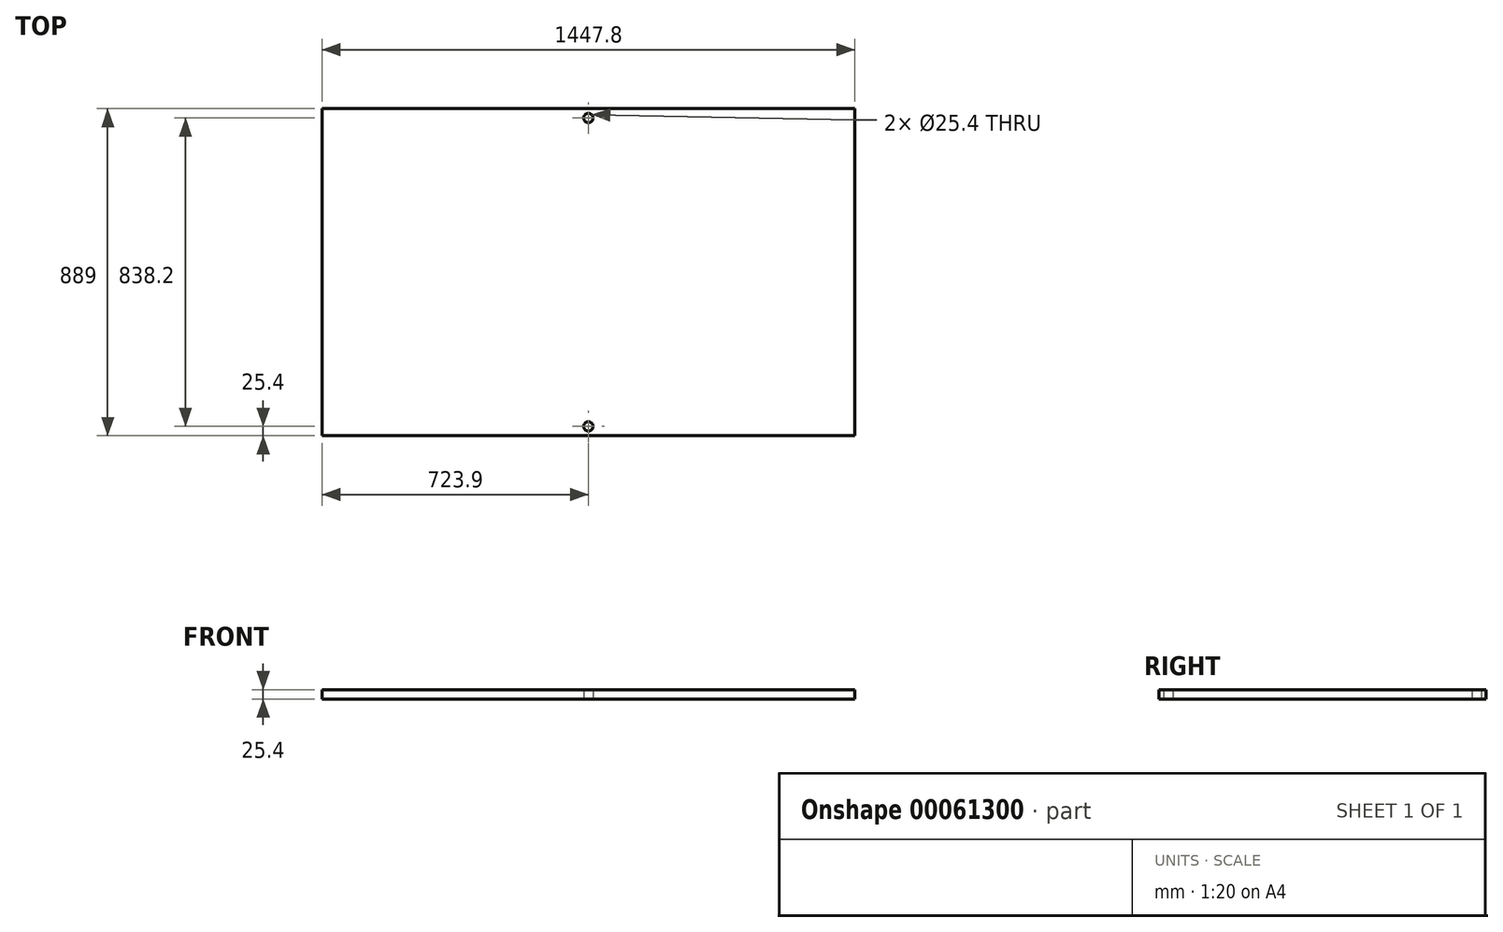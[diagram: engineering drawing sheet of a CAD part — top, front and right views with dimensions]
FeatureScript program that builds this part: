
annotation { "Feature Type Name" : "Feature", "Feature Type Description" : "" }
export const myFeature = defineFeature(function(context is Context, id is Id, definition is map)
    precondition{}
    {
        {
            var Q0;
            Q0=qCreatedBy(makeId("Top.planeOp"),FACE);
            var sketch = newSketch(context, id + "F0", { "sketchPlane" : qUnion([Q0])});
            skLineSegment(sketch, "E0.rect.bottom", {"start": v(723.9, 444.5) * mm, "end": v(-723.9, 444.5) * mm});
            skLineSegment(sketch, "E0.rect.top", {"start": v(723.9, -444.5) * mm, "end": v(-723.9, -444.5) * mm});
            skLineSegment(sketch, "E0.rect.left", {"start": v(723.9, 444.5) * mm, "end": v(723.9, -444.5) * mm});
            skLineSegment(sketch, "E0.rect.right", {"start": v(-723.9, 444.5) * mm, "end": v(-723.9, -444.5) * mm});
            skPoint(sketch, "E0.rect.middle", {"position": v(0, 0) * mm});
            skCircle(sketch, "E1", {"center": v(0, 419.1) * mm, "radius": 12.7 * mm});
            skCircle(sketch, "E2.MirrorC", {"center": v(0, -419.1) * mm, "radius": 12.7 * mm});
            skSolve(sketch);
        }
        {
            var Q0;
            Q0=makeQuery(id+"F0.imprint","IMPRINT",FACE,{"disambiguationData":[TD([[makeQuery(id+"F0.imprint","IMPRINT",EDGE,{"derivedFrom":sQuery(id+"F0.wireOp",EDGE,"E0.rect.bottom")}),1.0]])]});
            extrude(context, id + "F1", {"entities" : qUnion([Q0]), "depth" : 25.4 * mm});
        }
    });
